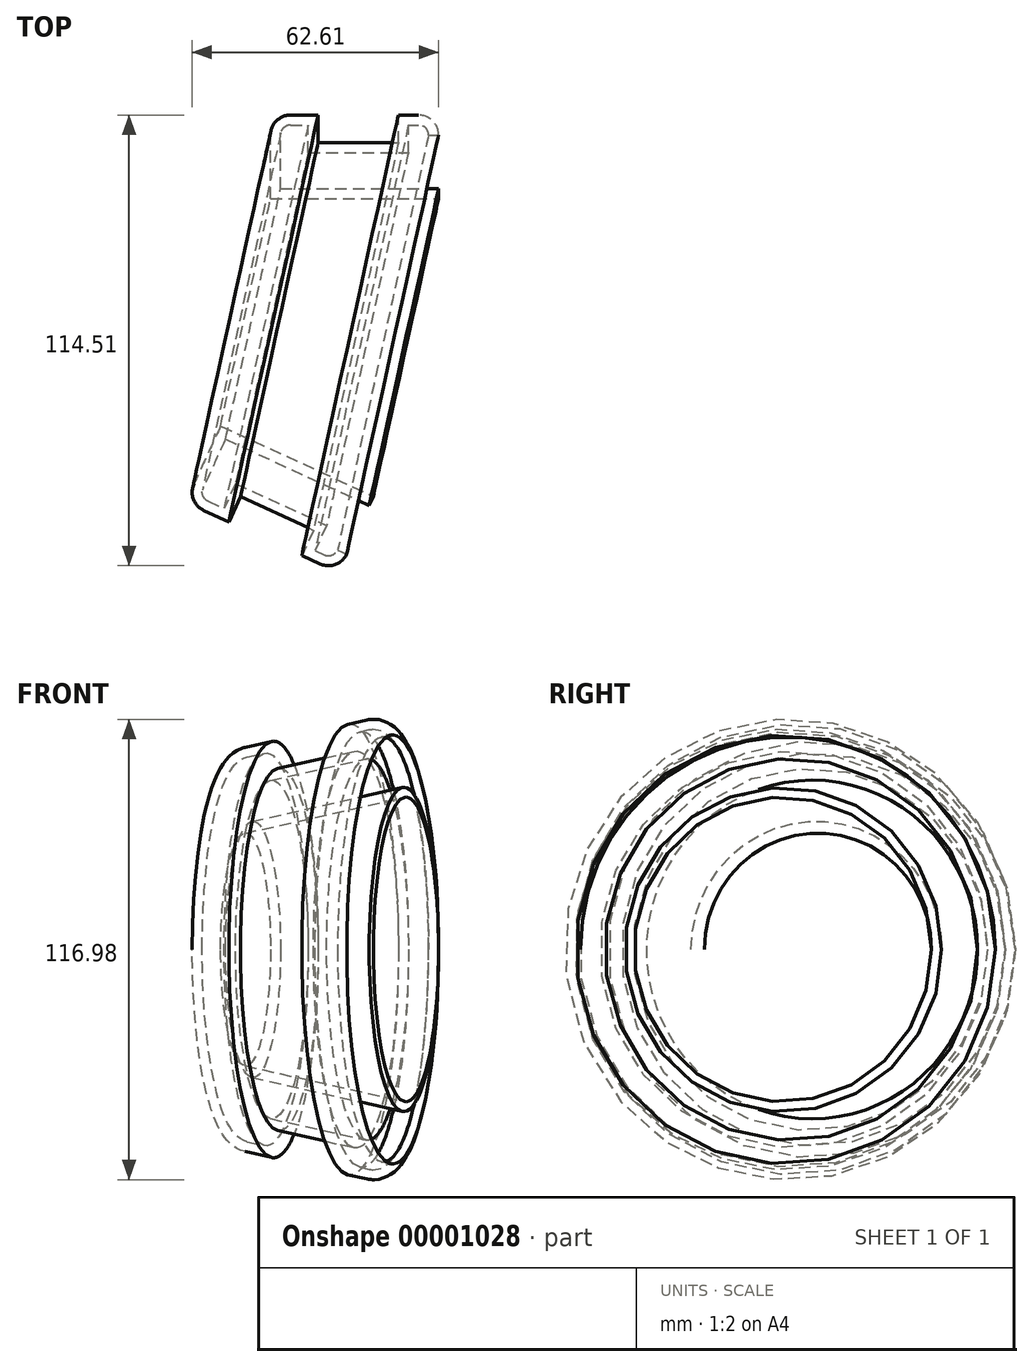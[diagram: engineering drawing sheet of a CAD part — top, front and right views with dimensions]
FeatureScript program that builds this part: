
annotation { "Feature Type Name" : "Feature", "Feature Type Description" : "" }
export const myFeature = defineFeature(function(context is Context, id is Id, definition is map)
    precondition{}
    {
        {
            var Q0;
            Q0=qCreatedBy(makeId("Top.planeOp"),FACE);
            var sketch = newSketch(context, id + "F0", { "sketchPlane" : qUnion([Q0])});
            skCircle(sketch, "E0", {"center": v(0, 0) * mm, "radius": 43.3 * mm});
            skCircle(sketch, "E1", {"center": v(-22.64, 13.1) * mm, "radius": 36.95 * mm});
            skCircle(sketch, "E2.cCircle", {"center": v(-38.17, -20.42) * mm, "radius": 21.94 * mm, "construction": true});
            skLineSegment(sketch, "E2.0", {"start": v(-54.14, -38) * mm, "end": v(-61.9, -21.57) * mm});
            skLineSegment(sketch, "E2.1", {"start": v(-61.9, -21.57) * mm, "end": v(-55.75, -4.46) * mm});
            skLineSegment(sketch, "E2.2", {"start": v(-55.75, -4.46) * mm, "end": v(-39.31, 3.3) * mm});
            skLineSegment(sketch, "E2.3", {"start": v(-39.31, 3.3) * mm, "end": v(-22.2, -2.84) * mm});
            skLineSegment(sketch, "E2.4", {"start": v(-22.2, -2.84) * mm, "end": v(-14.45, -19.28) * mm});
            skLineSegment(sketch, "E2.5", {"start": v(-14.45, -19.28) * mm, "end": v(-20.6, -36.39) * mm});
            skLineSegment(sketch, "E2.6", {"start": v(-20.6, -36.39) * mm, "end": v(-37.03, -44.14) * mm});
            skLineSegment(sketch, "E2.7", {"start": v(-37.03, -44.14) * mm, "end": v(-54.14, -38) * mm});
            skPoint(sketch, "E2.0.midPoint", {"position": v(-58.01, -29.79) * mm});
            skSolve(sketch);
        }
        {
            var Q0;
            {var subQ0=sQuery(id+"F0.wireOp",EDGE,"E2.2");var subQ1=sQuery(id+"F0.wireOp",EDGE,"E0");var subQ2=makeQuery(id+"F0.imprint","INTERSECT",VERTEX,{"derivedFrom":[subQ1,subQ0]});var subQ3=sQuery(id+"F0.wireOp",EDGE,"E1");var subQ6=makeQuery(id+"F0.imprint","INTERSECT",VERTEX,{"disambiguationData":[OD(0.0)],"derivedFrom":[subQ1,subQ3]});var subQ7=makeQuery(id+"F0.imprint","IMPRINT",EDGE,{"disambiguationData":[TD([[subQ6,-1.0]])],"derivedFrom":subQ1});var subQ9=sQuery(id+"F0.wireOp",EDGE,"E2.6");var subQ10=makeQuery(id+"F0.imprint","INTERSECT",VERTEX,{"derivedFrom":[subQ1,subQ9]});var subQ14=makeQuery(id+"F0.imprint","IMPRINT",EDGE,{"disambiguationData":[TD([[subQ10,1.0]])],"derivedFrom":subQ1});var subQ22=sQuery(id+"F0.wireOp",EDGE,"E2.3");Q0=qUnion([makeQuery(id+"F0.imprint","IMPRINT",FACE,{"disambiguationData":[TD([[subQ7,-1.0]])]}),makeQuery(id+"F0.imprint","IMPRINT",FACE,{"disambiguationData":[TD([[makeQuery(id+"F0.imprint","IMPRINT",EDGE,{"derivedFrom":sQuery(id+"F0.wireOp",EDGE,"E2.0")}),-1.0]])]}),makeQuery(id+"F0.imprint","IMPRINT",FACE,{"disambiguationData":[TD([[makeQuery(id+"F0.imprint","IMPRINT",EDGE,{"disambiguationData":[TD([[subQ6,1.0]])],"derivedFrom":subQ1}),1.0]])]}),makeQuery(id+"F0.imprint","IMPRINT",FACE,{"disambiguationData":[TD([[makeQuery(id+"F0.imprint","IMPRINT",EDGE,{"derivedFrom":subQ22}),1.0]])]}),makeQuery(id+"F0.imprint","IMPRINT",FACE,{"disambiguationData":[TD([[makeQuery(id+"F0.imprint","IMPRINT",EDGE,{"disambiguationData":[TD([[subQ2,-1.0]])],"derivedFrom":subQ1}),-1.0]])]}),makeQuery(id+"F0.imprint","IMPRINT",FACE,{"disambiguationData":[TD([[subQ14,1.0]])]})]);}
            var Q1;
            {var subQ4=sQuery(id+"F0.wireOp",EDGE,"E2.3");Q1=makeQuery(id+"F0.imprint","IMPRINT",FACE,{"disambiguationData":[TD([[makeQuery(id+"F0.imprint","IMPRINT",EDGE,{"derivedFrom":subQ4}),-1.0]])]});}
            extrude(context, id + "F1", {"entities" : qUnion([Q0, Q1]), "depth" : 25.4 * mm});
        }
        {
            var Q0;
            Q0=makeQuery(id+"F1.opExtrude","CAP_EDGE",EDGE,{"disambiguationData":[OSD([sQuery(id+"F0.wireOp",EDGE,"E2.0")])],"isStart":false});
            var Q1;
            Q1=makeQuery(id+"F1.opExtrude","CAP_EDGE",EDGE,{"disambiguationData":[OSD([sQuery(id+"F0.wireOp",EDGE,"E2.7")])],"isStart":false});
            var Q2;
            Q2=makeQuery(id+"F1.opExtrude","CAP_EDGE",EDGE,{"disambiguationData":[OSD([sQuery(id+"F0.wireOp",EDGE,"E2.6")])],"isStart":false});
            var Q3;
            Q3=makeQuery(id+"F1.opExtrude","CAP_EDGE",EDGE,{"disambiguationData":[OSD([sQuery(id+"F0.wireOp",EDGE,"E0")])],"isStart":false});
            var Q4;
            Q4=makeQuery(id+"F1.opExtrude","CAP_EDGE",EDGE,{"disambiguationData":[OSD([sQuery(id+"F0.wireOp",EDGE,"E1")])],"isStart":false});
            fillet(context, id + "F2", {"entities" : qUnion([Q0, Q1, Q2, Q3, Q4]), "radius" : 5.08 * mm, "tangentPropagation" : true, "allowEdgeOverflow" : false});
        }
        {
            var Q0;
            Q0=makeQuery(id+"F1.opExtrude","SWEPT_BODY",BODY,{"disambiguationData":[OSD([sQuery(id+"F0.wireOp",EDGE,"E0"),sQuery(id+"F0.wireOp",EDGE,"E1"),sQuery(id+"F0.wireOp",EDGE,"E2.0"),sQuery(id+"F0.wireOp",EDGE,"E2.1"),sQuery(id+"F0.wireOp",EDGE,"E2.2"),sQuery(id+"F0.wireOp",EDGE,"E2.6"),sQuery(id+"F0.wireOp",EDGE,"E2.7")])]});
            deleteBodies(context, id + "F3", {"entities" : qUnion([Q0])});
        }
        {
            var Q0;
            Q0=qCreatedBy(makeId("Top.planeOp"),FACE);
            var sketch = newSketch(context, id + "F4", { "sketchPlane" : qUnion([Q0])});
            skLineSegment(sketch, "E3.bottom", {"start": v(-19.52, 58.93) * mm, "end": v(23.19, 58.93) * mm});
            skLineSegment(sketch, "E3.top", {"start": v(-19.52, 37.67) * mm, "end": v(23.19, 37.67) * mm});
            skLineSegment(sketch, "E3.left", {"start": v(-19.52, 58.93) * mm, "end": v(-19.52, 37.67) * mm});
            skLineSegment(sketch, "E3.right", {"start": v(23.19, 58.93) * mm, "end": v(23.19, 37.67) * mm});
            skLineSegment(sketch, "E4.bottom", {"start": v(-7.41, 58.93) * mm, "end": v(12.98, 58.93) * mm});
            skLineSegment(sketch, "E4.top", {"start": v(-7.41, 51.9) * mm, "end": v(12.98, 51.9) * mm});
            skLineSegment(sketch, "E4.left", {"start": v(-7.41, 58.93) * mm, "end": v(-7.41, 51.9) * mm});
            skLineSegment(sketch, "E4.right", {"start": v(12.98, 58.93) * mm, "end": v(12.98, 51.9) * mm});
            skSolve(sketch);
        }
        {
            var Q0;
            Q0=qCreatedBy(makeId("Top.planeOp"),FACE);
            var sketch = newSketch(context, id + "F5", { "sketchPlane" : qUnion([Q0])});
            skLineSegment(sketch, "E5", {"start": v(102.5, -19.34) * mm, "end": v(-109.57, 27.16) * mm});
            skSolve(sketch);
        }
        {
            var Q0;
            Q0 = qSketchRegion(id + "F5", true);
            var Q1;
            Q1=makeQuery(id+"F4.imprint","IMPRINT",FACE,{"disambiguationData":[TD([[makeQuery(id+"F4.imprint","IMPRINT",EDGE,{"derivedFrom":sQuery(id+"F4.wireOp",EDGE,"E3.top")}),1.0]])]});
            var Q2;
            Q2=sQuery(id+"F5.wireOp",EDGE,"E5");
            revolve(context, id + "F6", {"entities" : qUnion([Q0, Q1]), "axis" : qUnion([Q2]), "revolveType" : RevolveType.FULL});
        }
        {
            var Q0;
            Q0=makeQuery(id+"F6.opRevolve","SWEPT_EDGE",EDGE,{"disambiguationData":[OSD([sQuery(id+"F4.wireOp",EDGE,"E3.bottom"),sQuery(id+"F4.wireOp",EDGE,"E3.left")])]});
            var Q1;
            Q1=makeQuery(id+"F6.opRevolve","SWEPT_EDGE",EDGE,{"disambiguationData":[OSD([sQuery(id+"F4.wireOp",EDGE,"E3.bottom"),sQuery(id+"F4.wireOp",EDGE,"E3.right")])]});
            fillet(context, id + "F7", {"entities" : qUnion([Q0, Q1]), "radius" : 5.08 * mm, "tangentPropagation" : true, "allowEdgeOverflow" : false});
        }
        {
            var Q0;
            Q0=makeQuery(id+"F6.opRevolve","SWEPT_FACE",FACE,{"disambiguationData":[OSD([sQuery(id+"F4.wireOp",EDGE,"E3.right")])]});
            shell(context, id + "F8", {"entities" : qUnion([Q0]), "thickness" : 2.54 * mm});
        }
        {
            var Q0;
            Q0=makeQuery(id+"F6.opRevolve","SWEPT_BODY",BODY,{"disambiguationData":[OSD([sQuery(id+"F4.wireOp",EDGE,"E3.bottom"),sQuery(id+"F4.wireOp",EDGE,"E3.top"),sQuery(id+"F4.wireOp",EDGE,"E3.left"),sQuery(id+"F4.wireOp",EDGE,"E3.right"),sQuery(id+"F4.wireOp",EDGE,"E4.top"),sQuery(id+"F4.wireOp",EDGE,"E4.left"),sQuery(id+"F4.wireOp",EDGE,"E4.right")])]});
            var Q1;
            Q1=qCreatedBy(makeId("Top.planeOp"),FACE);
            mirror(context, id + "F9", {"entities" : qUnion([Q0]), "mirrorPlane" : qUnion([Q1])});
        }
    });
